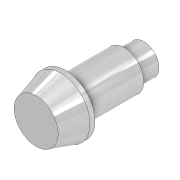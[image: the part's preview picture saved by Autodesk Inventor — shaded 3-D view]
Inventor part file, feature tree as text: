
AUTODESK INVENTOR PART (.ipt)
format: ipt  version: 2022 (Build 260153000, 153)  size: 109,568 bytes
history: native  units: mm
features: sketch x5, extrude x3, plane x1, loft x1, projected_geometry x1
ambient origin geometry x8: Origin, YZ Plane, XZ Plane, XY Plane, X Axis, Y Axis, Z Axis, Center Point
bodies: Solid1 (feature_tree)
feature tree (11):
  sketch  "Sketch2"  dims[d0=12.0mm d1=5.0mm]
  plane  "Work Plane1"
  loft  "Loft1"
  extrude  "Extrusion1"  TaperAngle=0.0deg  [1 undecoded]
  extrude  "Extrusion2"  Depth=1.0mm TaperAngle=0.0deg
  extrude  "Extrusion3"  Depth=12.0mm TaperAngle=0.0deg
  sketch  "Sketch3"  dims[d2=9.0mm d3=0.0mm d4=90.0deg]
  sketch  "Sketch4"  dims[d5=0.0mm d6=90.0deg d7=1.0mm d8=0.0mm]
  sketch  "Sketch5"  dims[d9=8.0mm d10=12.0mm d11=0.0mm]
  sketch  "Sketch6"  dims[d12=6.2mm d13=4.0mm d14=0.0mm]
  projected_geometry  "Project Cut Edges1"
note: 1 required parameter value undecoded (feature->parameter linkage not recoverable at this tier; creation-order binding heuristic only, values carry confidence <= 0.55)
